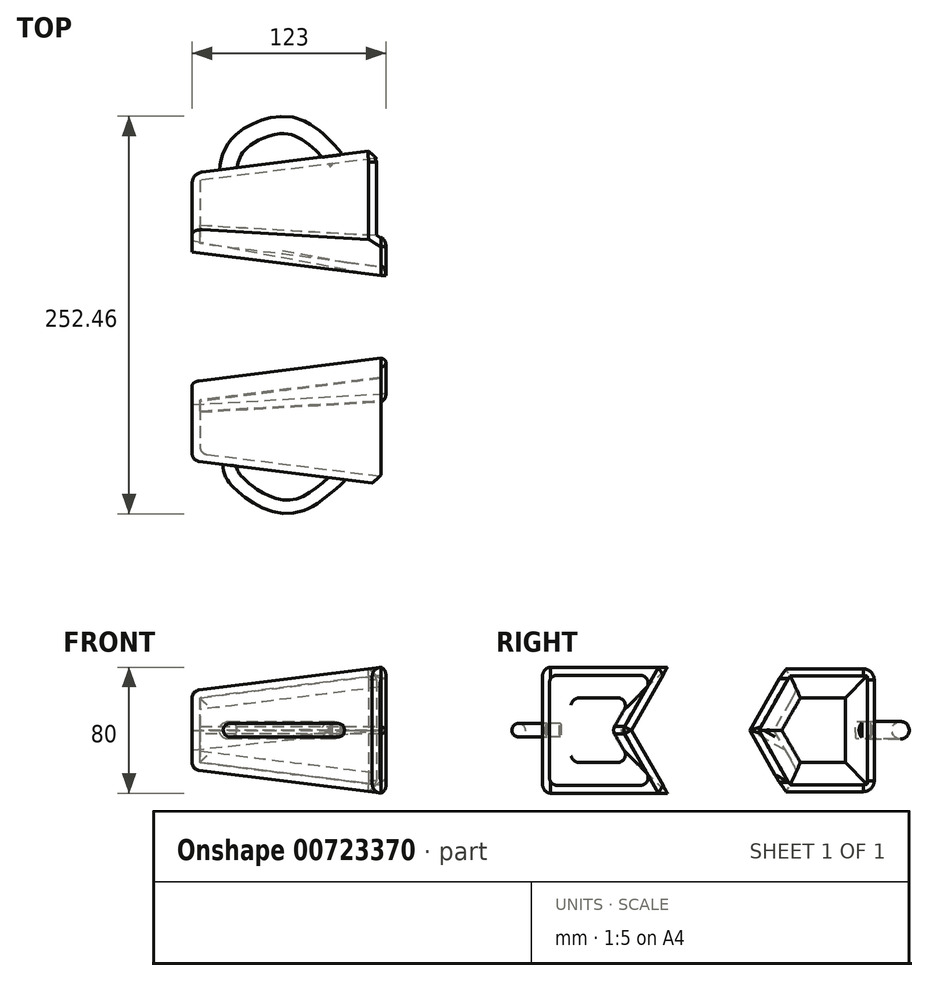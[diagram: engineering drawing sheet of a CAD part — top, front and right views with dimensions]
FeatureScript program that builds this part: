
annotation { "Feature Type Name" : "Feature", "Feature Type Description" : "" }
export const myFeature = defineFeature(function(context is Context, id is Id, definition is map)
    precondition{}
    {
        {
            var Q0;
            Q0=qCreatedBy(makeId("Right.planeOp"),FACE);
            cPlane(context, id + "F0", {"entities" : qUnion([Q0]), "cplaneType" : CPlaneType.OFFSET, "offset" : 120 * mm, "width" : 150 * mm, "height" : 150 * mm});
        }
        {
            var Q0;
            Q0=qCreatedBy(makeId("Right.planeOp"),FACE);
            var sketch = newSketch(context, id + "F1", { "sketchPlane" : qUnion([Q0])});
            skLineSegment(sketch, "E0.bottom", {"start": v(25, -25) * mm, "end": v(-25, -25) * mm});
            skLineSegment(sketch, "E0.top", {"start": v(25, 25) * mm, "end": v(-25, 25) * mm});
            skLineSegment(sketch, "E0.right", {"start": v(-25, -25) * mm, "end": v(-25, 25) * mm});
            skLineSegment(sketch, "E1.bottom", {"start": v(157.4, -25) * mm, "end": v(121.9, -25) * mm});
            skLineSegment(sketch, "E1.top", {"start": v(157.4, 25) * mm, "end": v(121.9, 25) * mm});
            skLineSegment(sketch, "E1.left", {"start": v(157.4, -25) * mm, "end": v(157.4, 25) * mm});
            skLineSegment(sketch, "E2", {"start": v(25, 25) * mm, "end": v(10.59, 0) * mm});
            skLineSegment(sketch, "E3", {"start": v(10.59, 0) * mm, "end": v(25, -25) * mm});
            skLineSegment(sketch, "E4.1.0.0", {"start": v(107.49, 0) * mm, "end": v(121.9, -25) * mm});
            skLineSegment(sketch, "E4.1.0.1", {"start": v(121.9, 25) * mm, "end": v(107.49, 0) * mm});
            skSolve(sketch);
        }
        {
            var Q0;
            Q0=qCreatedBy(id+"F0.planeOp",FACE);
            var sketch = newSketch(context, id + "F2", { "sketchPlane" : qUnion([Q0])});
            skLineSegment(sketch, "E5.bottom", {"start": v(-40, 40) * mm, "end": v(40, 40) * mm});
            skLineSegment(sketch, "E5.top", {"start": v(-40, -40) * mm, "end": v(40, -40) * mm});
            skLineSegment(sketch, "E5.left", {"start": v(-40, 40) * mm, "end": v(-40, -40) * mm});
            skPoint(sketch, "E5.middle", {"position": v(0, 0) * mm});
            skLineSegment(sketch, "E6.bottom", {"start": v(115, 40) * mm, "end": v(172.4, 40) * mm});
            skLineSegment(sketch, "E6.top", {"start": v(115, -40) * mm, "end": v(172.4, -40) * mm});
            skLineSegment(sketch, "E6.left", {"start": v(92.4, 0.1) * mm, "end": v(92.4, -0.1) * mm});
            skLineSegment(sketch, "E6.right", {"start": v(172.4, 40) * mm, "end": v(172.4, -40) * mm});
            skLineSegment(sketch, "E7", {"start": v(40, 40) * mm, "end": v(17.35, 0) * mm});
            skLineSegment(sketch, "E8", {"start": v(17.35, 0) * mm, "end": v(40, -40) * mm});
            skLineSegment(sketch, "E9.1.0.0", {"start": v(115, 40) * mm, "end": v(92.35, 0) * mm});
            skLineSegment(sketch, "E9.1.0.1", {"start": v(92.35, 0) * mm, "end": v(115, -40) * mm});
            skSolve(sketch);
        }
        {
            var Q0;
            Q0=makeQuery(id+"F1.imprint","IMPRINT",FACE,{"disambiguationData":[TD([[makeQuery(id+"F1.imprint","IMPRINT",EDGE,{"derivedFrom":sQuery(id+"F1.wireOp",EDGE,"E0.bottom")}),-1.0]])]});
            var Q1;
            Q1=makeQuery(id+"F2.imprint","IMPRINT",FACE,{"disambiguationData":[TD([[makeQuery(id+"F2.imprint","IMPRINT",EDGE,{"derivedFrom":sQuery(id+"F2.wireOp",EDGE,"E5.bottom")}),-1.0]])]});
            var Q2;
            Q2=sQuery(id+"F2.wireOp",VERTEX,"E5.top.end");
            var Q3;
            Q3=sQuery(id+"F45uSzDcTnPupgU_0.wireOp",VERTEX,"yKV4fNBH-vfpY-PDVQ-35ui-MYD5tKzPFPvu.end");
            loft(context, id + "F3", {"sheetProfilesArray" : [{ "sheetProfileEntities" : qUnion([Q0]) }, { "sheetProfileEntities" : qUnion([Q1]) }], "connections" : [{ "connectionEntities" : qUnion([Q2, Q3]), "connectionEdgeQueries" : qUnion([]), "connectionEdgeParameters" : [] }]});
        }
        {
            var Q0;
            Q0=makeQuery(id+"F1.imprint","IMPRINT",FACE,{"disambiguationData":[TD([[makeQuery(id+"F1.imprint","IMPRINT",EDGE,{"derivedFrom":sQuery(id+"F1.wireOp",EDGE,"E1.bottom")}),-1.0]])]});
            var Q1;
            {var subQ2=sQuery(id+"F2.wireOp",EDGE,"E6.bottom");Q1=makeQuery(id+"F2.imprint","IMPRINT",FACE,{"disambiguationData":[TD([[makeQuery(id+"F2.imprint","IMPRINT",EDGE,{"derivedFrom":subQ2}),-1.0]])]});}
            var Q2;
            Q2=sQuery(id+"F2.wireOp",VERTEX,"E6.bottom.start");
            var Q3;
            Q3=sQuery(id+"F1.wireOp",VERTEX,"E1.top.end");
            loft(context, id + "F4", {"sheetProfilesArray" : [{ "sheetProfileEntities" : qUnion([Q0]) }, { "sheetProfileEntities" : qUnion([Q1]) }], "matchConnections" : true, "connections" : [{ "connectionEntities" : qUnion([Q2, Q3]), "connectionEdgeQueries" : qUnion([]), "connectionEdgeParameters" : [] }]});
        }
        {
            var Q0;
            {var subQ2=sQuery(id+"F2.wireOp",EDGE,"E6.bottom");Q0=makeQuery(id+"F4.opLoft","CAP_FACE",FACE,{"disambiguationData":[OSD([makeQuery(id+"F2.imprint","IMPRINT",FACE,{"disambiguationData":[TD([[makeQuery(id+"F2.imprint","IMPRINT",EDGE,{"derivedFrom":subQ2}),-1.0]])]})])],"isStart":true});}
            shell(context, id + "F5", {"entities" : qUnion([Q0]), "thickness" : 5 * mm});
        }
        {
            var Q0;
            Q0=makeQuery(id+"F3.opLoft","CAP_FACE",FACE,{"disambiguationData":[OSD([makeQuery(id+"F2.imprint","IMPRINT",FACE,{"disambiguationData":[TD([[makeQuery(id+"F2.imprint","IMPRINT",EDGE,{"derivedFrom":sQuery(id+"F2.wireOp",EDGE,"E5.bottom")}),-1.0]])]})])],"isStart":true});
            shell(context, id + "F6", {"entities" : qUnion([Q0]), "thickness" : 5 * mm});
        }
        {
            var Q0;
            Q0=makeQuery(id+"F4.opLoft","SWEPT_EDGE",EDGE,{"disambiguationData":[OSD([sQuery(id+"F1.wireOp",EDGE,"E1.top"),sQuery(id+"F1.wireOp",EDGE,"E1.left"),sQuery(id+"F2.wireOp",EDGE,"E6.bottom"),sQuery(id+"F2.wireOp",EDGE,"E6.right")])]});
            var Q1;
            Q1=makeQuery(id+"F4.opLoft","SWEPT_EDGE",EDGE,{"disambiguationData":[OSD([sQuery(id+"F1.wireOp",EDGE,"E1.bottom"),sQuery(id+"F1.wireOp",EDGE,"E1.left"),sQuery(id+"F2.wireOp",EDGE,"E6.top"),sQuery(id+"F2.wireOp",EDGE,"E6.right")])]});
            var Q2;
            Q2=makeQuery(id+"F4.opLoft","MID_CAP_EDGE",EDGE,{"disambiguationData":[OSD([sQuery(id+"F1.wireOp",EDGE,"E1.bottom"),sQuery(id+"F1.wireOp",EDGE,"E1.top"),sQuery(id+"F1.wireOp",EDGE,"E1.left")])],"capPos":0.0});
            var Q3;
            Q3=makeQuery(id+"F4.opLoft","MID_CAP_EDGE",EDGE,{"disambiguationData":[OSD([sQuery(id+"F1.wireOp",EDGE,"E1.top"),sQuery(id+"F1.wireOp",EDGE,"E1.left"),sQuery(id+"F1.wireOp",EDGE,"E4.1.0.1")])],"capPos":0.0});
            var Q4;
            Q4=makeQuery(id+"F4.opLoft","MID_CAP_EDGE",EDGE,{"disambiguationData":[OSD([sQuery(id+"F1.wireOp",EDGE,"E1.bottom"),sQuery(id+"F1.wireOp",EDGE,"E1.left"),sQuery(id+"F1.wireOp",EDGE,"E4.1.0.0")])],"capPos":0.0});
            fillet(context, id + "F7", {"entities" : qUnion([Q0, Q1, Q2, Q3, Q4]), "radius" : 7 * mm, "tangentPropagation" : true, "allowEdgeOverflow" : false});
        }
        {
            var Q0;
            Q0=makeQuery(id+"F4.opLoft","MID_CAP_EDGE",EDGE,{"disambiguationData":[OSD([sQuery(id+"F2.wireOp",EDGE,"E6.bottom"),sQuery(id+"F2.wireOp",EDGE,"E6.top"),sQuery(id+"F2.wireOp",EDGE,"E6.right")])],"capPos":1.0});
            var Q1;
            Q1=makeQuery(id+"F4.opLoft","MID_CAP_EDGE",EDGE,{"disambiguationData":[OSD([sQuery(id+"F2.wireOp",EDGE,"E6.bottom"),sQuery(id+"F2.wireOp",EDGE,"E6.right"),sQuery(id+"F2.wireOp",EDGE,"E9.1.0.0")])],"capPos":1.0});
            var Q2;
            Q2=makeQuery(id+"F4.opLoft","MID_CAP_EDGE",EDGE,{"disambiguationData":[OSD([sQuery(id+"F2.wireOp",EDGE,"E6.top"),sQuery(id+"F2.wireOp",EDGE,"E6.right"),sQuery(id+"F2.wireOp",EDGE,"E9.1.0.1")])],"capPos":1.0});
            var Q3;
            {var subQ0=sQuery(id+"F2.wireOp",EDGE,"E6.right");var subQ2=sQuery(id+"F2.wireOp",EDGE,"E6.top");var subQ3=sQuery(id+"F2.wireOp",EDGE,"E6.bottom");Q3=makeQuery(id+"F7.opFillet","BLEND_EDGE",EDGE,{"blendedFrom":[makeQuery(id+"F4.opLoft","SWEPT_EDGE",EDGE,{"disambiguationData":[OSD([sQuery(id+"F1.wireOp",EDGE,"E1.bottom"),sQuery(id+"F1.wireOp",EDGE,"E1.left"),subQ2,subQ0])]}),makeQuery(id+"F4.opLoft","CAP_FACE",FACE,{"disambiguationData":[OSD([makeQuery(id+"F2.imprint","IMPRINT",FACE,{"disambiguationData":[TD([[makeQuery(id+"F2.imprint","IMPRINT",EDGE,{"derivedFrom":subQ3}),-1.0]])]})])],"isStart":true})],"blendedInto":[makeQuery(id+"F4.opLoft","CAP_FACE",FACE,{"disambiguationData":[OSD([makeQuery(id+"F2.imprint","IMPRINT",FACE,{"disambiguationData":[TD([[makeQuery(id+"F2.imprint","IMPRINT",EDGE,{"derivedFrom":subQ3}),-1.0]])]})])],"isStart":true})]});}
            var Q4;
            {var subQ0=sQuery(id+"F2.wireOp",EDGE,"E6.right");var subQ3=sQuery(id+"F2.wireOp",EDGE,"E6.bottom");Q4=makeQuery(id+"F7.opFillet","BLEND_EDGE",EDGE,{"blendedFrom":[makeQuery(id+"F4.opLoft","SWEPT_EDGE",EDGE,{"disambiguationData":[OSD([sQuery(id+"F1.wireOp",EDGE,"E1.top"),sQuery(id+"F1.wireOp",EDGE,"E1.left"),subQ3,subQ0])]}),makeQuery(id+"F4.opLoft","CAP_FACE",FACE,{"disambiguationData":[OSD([makeQuery(id+"F2.imprint","IMPRINT",FACE,{"disambiguationData":[TD([[makeQuery(id+"F2.imprint","IMPRINT",EDGE,{"derivedFrom":subQ3}),-1.0]])]})])],"isStart":true})],"blendedInto":[makeQuery(id+"F4.opLoft","CAP_FACE",FACE,{"disambiguationData":[OSD([makeQuery(id+"F2.imprint","IMPRINT",FACE,{"disambiguationData":[TD([[makeQuery(id+"F2.imprint","IMPRINT",EDGE,{"derivedFrom":subQ3}),-1.0]])]})])],"isStart":true})]});}
            chamfer(context, id + "F8", {"entities" : qUnion([Q0, Q1, Q2, Q3, Q4]), "width" : 7 * mm, "tangentPropagation" : true});
        }
        {
            var Q0;
            Q0=qCreatedBy(id+"F0.planeOp",FACE);
            var sketch = newSketch(context, id + "F9", { "sketchPlane" : qUnion([Q0])});
            skLineSegment(sketch, "E10", {"start": v(40, -40) * mm, "end": v(17.35, 0) * mm});
            skLineSegment(sketch, "E11", {"start": v(17.35, 0) * mm, "end": v(40, 40) * mm});
            skLineSegment(sketch, "E12", {"start": v(40, 40) * mm, "end": v(34.25, 40) * mm});
            skLineSegment(sketch, "E13", {"start": v(34.25, 40) * mm, "end": v(11.6, 0) * mm});
            skLineSegment(sketch, "E14", {"start": v(11.6, 0) * mm, "end": v(34.25, -40) * mm});
            skLineSegment(sketch, "E15", {"start": v(34.25, -40) * mm, "end": v(40, -40) * mm});
            skLineSegment(sketch, "E16", {"start": v(116.82, -33) * mm, "end": v(98.13, 0) * mm});
            skLineSegment(sketch, "E17", {"start": v(98.13, 0) * mm, "end": v(116.82, 33) * mm});
            skLineSegment(sketch, "E18", {"start": v(116.82, 33) * mm, "end": v(111.04, 33) * mm});
            skLineSegment(sketch, "E19", {"start": v(111.04, 33) * mm, "end": v(92.35, 0) * mm});
            skLineSegment(sketch, "E20", {"start": v(92.35, 0) * mm, "end": v(111.04, -33) * mm});
            skLineSegment(sketch, "E21", {"start": v(111.04, -33) * mm, "end": v(116.82, -33) * mm});
            skSolve(sketch);
        }
        {
            var Q0;
            Q0 = qSketchRegion(id + "F9", true);
            extrude(context, id + "F10", {"entities" : qUnion([Q0]), "depth" : 3 * mm, "offsetDistance" : 25 * mm});
        }
        {
            var Q0;
            Q0=makeQuery(id+"F10.opExtrude","CAP_EDGE",EDGE,{"disambiguationData":[OSD([sQuery(id+"F9.wireOp",EDGE,"E16")])],"isStart":false});
            var Q1;
            Q1=makeQuery(id+"F10.opExtrude","CAP_EDGE",EDGE,{"disambiguationData":[OSD([sQuery(id+"F9.wireOp",EDGE,"E17")])],"isStart":false});
            var Q2;
            Q2=makeQuery(id+"F10.opExtrude","CAP_EDGE",EDGE,{"disambiguationData":[OSD([sQuery(id+"F9.wireOp",EDGE,"E21")])],"isStart":false});
            var Q3;
            Q3=makeQuery(id+"F10.opExtrude","CAP_EDGE",EDGE,{"disambiguationData":[OSD([sQuery(id+"F9.wireOp",EDGE,"E13")])],"isStart":false});
            var Q4;
            Q4=makeQuery(id+"F10.opExtrude","CAP_EDGE",EDGE,{"disambiguationData":[OSD([sQuery(id+"F9.wireOp",EDGE,"E14")])],"isStart":false});
            var Q5;
            Q5=makeQuery(id+"F10.opExtrude","CAP_EDGE",EDGE,{"disambiguationData":[OSD([sQuery(id+"F9.wireOp",EDGE,"E12")])],"isStart":false});
            var Q6;
            Q6=makeQuery(id+"F10.opExtrude","CAP_EDGE",EDGE,{"disambiguationData":[OSD([sQuery(id+"F9.wireOp",EDGE,"E15")])],"isStart":false});
            fillet(context, id + "F11", {"entities" : qUnion([Q0, Q1, Q2, Q3, Q4, Q5, Q6]), "radius" : 5 * mm, "tangentPropagation" : true, "allowEdgeOverflow" : false});
        }
        {
            var Q0;
            Q0=makeQuery(id+"F6.opShell","OFFSET_EDGE",EDGE,{"disambiguationData":[OSD([sQuery(id+"F1.wireOp",EDGE,"E0.top"),sQuery(id+"F1.wireOp",EDGE,"E0.right"),sQuery(id+"F2.wireOp",EDGE,"E5.bottom"),sQuery(id+"F2.wireOp",EDGE,"E5.left")])]});
            var Q1;
            Q1=makeQuery(id+"F6.opShell","OFFSET_EDGE",EDGE,{"disambiguationData":[OSD([sQuery(id+"F1.wireOp",EDGE,"E0.bottom"),sQuery(id+"F1.wireOp",EDGE,"E0.top"),sQuery(id+"F1.wireOp",EDGE,"E0.right")])]});
            var Q2;
            Q2=makeQuery(id+"F6.opShell","OFFSET_EDGE",EDGE,{"disambiguationData":[OSD([sQuery(id+"F1.wireOp",EDGE,"E0.bottom"),sQuery(id+"F1.wireOp",EDGE,"E0.right"),sQuery(id+"F2.wireOp",EDGE,"E5.top"),sQuery(id+"F2.wireOp",EDGE,"E5.left")])]});
            var Q3;
            Q3=makeQuery(id+"F6.opShell","OFFSET_EDGE",EDGE,{"disambiguationData":[OSD([sQuery(id+"F1.wireOp",EDGE,"E0.bottom"),sQuery(id+"F1.wireOp",EDGE,"E3"),sQuery(id+"F2.wireOp",EDGE,"E5.top"),sQuery(id+"F2.wireOp",EDGE,"E8")])]});
            var Q4;
            Q4=makeQuery(id+"F6.opShell","OFFSET_EDGE",EDGE,{"disambiguationData":[OSD([sQuery(id+"F1.wireOp",EDGE,"E2"),sQuery(id+"F1.wireOp",EDGE,"E3"),sQuery(id+"F2.wireOp",EDGE,"E7"),sQuery(id+"F2.wireOp",EDGE,"E8")])]});
            var Q5;
            Q5=makeQuery(id+"F6.opShell","OFFSET_EDGE",EDGE,{"disambiguationData":[OSD([sQuery(id+"F1.wireOp",EDGE,"E0.top"),sQuery(id+"F1.wireOp",EDGE,"E2"),sQuery(id+"F2.wireOp",EDGE,"E5.bottom"),sQuery(id+"F2.wireOp",EDGE,"E7")])]});
            var Q6;
            Q6=makeQuery(id+"F11.opFillet","BLEND_EDGE",EDGE,{"blendedFrom":[makeQuery(id+"F10.opExtrude","CAP_EDGE",EDGE,{"disambiguationData":[OSD([sQuery(id+"F9.wireOp",EDGE,"E13")])],"isStart":false}),makeQuery(id+"F10.opExtrude","CAP_EDGE",EDGE,{"disambiguationData":[OSD([sQuery(id+"F9.wireOp",EDGE,"E14")])],"isStart":false})],"blendedInto":[]});
            fillet(context, id + "F12", {"entities" : qUnion([Q0, Q1, Q2, Q3, Q4, Q5, Q6]), "radius" : 5 * mm, "tangentPropagation" : true, "allowEdgeOverflow" : false});
        }
        {
            var Q0;
            Q0=makeQuery(id+"F5.opShell","OFFSET_EDGE",EDGE,{"disambiguationData":[OSD([sQuery(id+"F1.wireOp",EDGE,"E4.1.0.0"),sQuery(id+"F1.wireOp",EDGE,"E4.1.0.1"),sQuery(id+"F2.wireOp",EDGE,"E6.left"),sQuery(id+"F2.wireOp",EDGE,"E9.1.0.1")])]});
            var Q1;
            {var subQ0=sQuery(id+"F2.wireOp",EDGE,"E6.left");Q1=makeQuery(id+"F5.opShell","SHELL_CAP_EDGE",EDGE,{"derivedFrom":[makeQuery(id+"F4.opLoft","MID_CAP_VERTEX",VERTEX,{"disambiguationData":[OSD([subQ0,sQuery(id+"F2.wireOp",EDGE,"E9.1.0.0")])],"capPos":1.0}),makeQuery(id+"F4.opLoft","MID_CAP_VERTEX",VERTEX,{"disambiguationData":[OSD([subQ0,sQuery(id+"F2.wireOp",EDGE,"E9.1.0.1")])],"capPos":1.0})]});}
            var Q2;
            Q2=makeQuery(id+"F11.opFillet","BLEND_EDGE",EDGE,{"blendedFrom":[makeQuery(id+"F10.opExtrude","CAP_EDGE",EDGE,{"disambiguationData":[OSD([sQuery(id+"F9.wireOp",EDGE,"E16")])],"isStart":false}),makeQuery(id+"F10.opExtrude","CAP_EDGE",EDGE,{"disambiguationData":[OSD([sQuery(id+"F9.wireOp",EDGE,"E17")])],"isStart":false})],"blendedInto":[]});
            var Q3;
            {var subQ0=sQuery(id+"F2.wireOp",EDGE,"E9.1.0.0");var subQ1=sQuery(id+"F2.wireOp",EDGE,"E6.bottom");var subQ2=sQuery(id+"F1.wireOp",EDGE,"E4.1.0.1");var subQ3=sQuery(id+"F1.wireOp",EDGE,"E1.top");Q3=makeQuery(id+"F5.opShell","OFFSET_EDGE",EDGE,{"disambiguationData":[OSD([subQ3,subQ2,subQ1,subQ0]),TDD([makeQuery(id+"F4.opLoft","SWEPT_EDGE",EDGE,{"disambiguationData":[OSD([subQ3,subQ2,subQ1,subQ0])]})])]});}
            var Q4;
            Q4=makeQuery(id+"F5.opShell","OFFSET_EDGE",EDGE,{"disambiguationData":[OSD([sQuery(id+"F1.wireOp",EDGE,"E1.bottom"),sQuery(id+"F1.wireOp",EDGE,"E4.1.0.0"),sQuery(id+"F2.wireOp",EDGE,"E6.top"),sQuery(id+"F2.wireOp",EDGE,"E9.1.0.1")])]});
            var Q5;
            Q5=makeQuery(id+"F5.opShell","OFFSET_EDGE",EDGE,{"disambiguationData":[OSD([sQuery(id+"F1.wireOp",EDGE,"E1.bottom"),sQuery(id+"F1.wireOp",EDGE,"E1.left"),sQuery(id+"F2.wireOp",EDGE,"E6.top"),sQuery(id+"F2.wireOp",EDGE,"E6.right")])]});
            var Q6;
            Q6=makeQuery(id+"F5.opShell","OFFSET_EDGE",EDGE,{"disambiguationData":[OSD([sQuery(id+"F1.wireOp",EDGE,"E1.top"),sQuery(id+"F1.wireOp",EDGE,"E1.left"),sQuery(id+"F2.wireOp",EDGE,"E6.bottom"),sQuery(id+"F2.wireOp",EDGE,"E6.right")])]});
            fillet(context, id + "F13", {"entities" : qUnion([Q0, Q1, Q2, Q3, Q4, Q5, Q6]), "radius" : 5 * mm, "tangentPropagation" : true, "allowEdgeOverflow" : false});
        }
        {
            var Q0;
            Q0=makeQuery(id+"F3.opLoft","MID_CAP_EDGE",EDGE,{"disambiguationData":[OSD([sQuery(id+"F2.wireOp",EDGE,"E5.bottom"),sQuery(id+"F2.wireOp",EDGE,"E5.top"),sQuery(id+"F2.wireOp",EDGE,"E5.left")])],"capPos":1.0});
            chamfer(context, id + "F14", {"entities" : qUnion([Q0]), "width" : 5 * mm, "tangentPropagation" : true});
        }
        {
            var Q0;
            Q0=makeQuery(id+"F3.opLoft","SWEPT_EDGE",EDGE,{"disambiguationData":[OSD([sQuery(id+"F1.wireOp",EDGE,"E0.top"),sQuery(id+"F1.wireOp",EDGE,"E0.right"),sQuery(id+"F2.wireOp",EDGE,"E5.bottom"),sQuery(id+"F2.wireOp",EDGE,"E5.left")])]});
            var Q1;
            {var subQ0=sQuery(id+"F2.wireOp",EDGE,"E5.left");var subQ1=sQuery(id+"F2.wireOp",EDGE,"E5.bottom");Q1=makeQuery(id+"F14.opChamfer","BLEND_EDGE",EDGE,{"blendedFrom":[makeQuery(id+"F3.opLoft","MID_CAP_EDGE",EDGE,{"disambiguationData":[OSD([subQ1,subQ0,sQuery(id+"F2.wireOp",EDGE,"E7")])],"capPos":1.0}),makeQuery(id+"F3.opLoft","MID_CAP_EDGE",EDGE,{"disambiguationData":[OSD([subQ1,sQuery(id+"F2.wireOp",EDGE,"E5.top"),subQ0])],"capPos":1.0})],"blendedInto":[]});}
            var Q2;
            {var subQ0=sQuery(id+"F2.wireOp",EDGE,"E5.left");var subQ1=sQuery(id+"F2.wireOp",EDGE,"E5.top");Q2=makeQuery(id+"F14.opChamfer","BLEND_EDGE",EDGE,{"blendedFrom":[makeQuery(id+"F3.opLoft","MID_CAP_EDGE",EDGE,{"disambiguationData":[OSD([sQuery(id+"F2.wireOp",EDGE,"E5.bottom"),subQ1,subQ0])],"capPos":1.0}),makeQuery(id+"F3.opLoft","MID_CAP_EDGE",EDGE,{"disambiguationData":[OSD([subQ1,subQ0,sQuery(id+"F2.wireOp",EDGE,"E8")])],"capPos":1.0})],"blendedInto":[]});}
            var Q3;
            Q3=makeQuery(id+"F3.opLoft","SWEPT_EDGE",EDGE,{"disambiguationData":[OSD([sQuery(id+"F1.wireOp",EDGE,"E0.bottom"),sQuery(id+"F1.wireOp",EDGE,"E0.right"),sQuery(id+"F2.wireOp",EDGE,"E5.top"),sQuery(id+"F2.wireOp",EDGE,"E5.left")])]});
            fillet(context, id + "F15", {"entities" : qUnion([Q0, Q1, Q2, Q3]), "radius" : 5 * mm, "tangentPropagation" : true, "allowEdgeOverflow" : false});
        }
        {
            var Q0;
            Q0=makeQuery(id+"F3.opLoft","MID_CAP_EDGE",EDGE,{"disambiguationData":[OSD([sQuery(id+"F1.wireOp",EDGE,"E0.top"),sQuery(id+"F1.wireOp",EDGE,"E0.right"),sQuery(id+"F1.wireOp",EDGE,"E2")])],"capPos":0.0});
            var Q1;
            Q1=makeQuery(id+"F3.opLoft","MID_CAP_EDGE",EDGE,{"disambiguationData":[OSD([sQuery(id+"F1.wireOp",EDGE,"E0.bottom"),sQuery(id+"F1.wireOp",EDGE,"E0.top"),sQuery(id+"F1.wireOp",EDGE,"E0.right")])],"capPos":0.0});
            var Q2;
            Q2=makeQuery(id+"F3.opLoft","MID_CAP_EDGE",EDGE,{"disambiguationData":[OSD([sQuery(id+"F1.wireOp",EDGE,"E0.bottom"),sQuery(id+"F1.wireOp",EDGE,"E0.right"),sQuery(id+"F1.wireOp",EDGE,"E3")])],"capPos":0.0});
            fillet(context, id + "F16", {"entities" : qUnion([Q0, Q1, Q2]), "radius" : 5 * mm, "tangentPropagation" : true, "allowEdgeOverflow" : false});
        }
        {
            var Q0;
            Q0=qCreatedBy(makeId("Top.planeOp"),FACE);
            var sketch = newSketch(context, id + "F17", { "sketchPlane" : qUnion([Q0])});
            skFitSpline(sketch, "E22", {"points": [v(93.6, -34.42) * mm, v(58.66, -54.04) * mm, v(26.5, -34.89) * mm, v(24.46, -27.36) * mm], "startDerivative": vector(-74.83, -69.14) * mm, "endDerivative": vector(0.53, 35.46) * mm});
            skSolve(sketch);
        }
        {
            var Q0;
            Q0=qCreatedBy(makeId("Front.planeOp"),FACE);
            cPlane(context, id + "F18", {"entities" : qUnion([Q0]), "cplaneType" : CPlaneType.OFFSET, "offset" : 29 * mm, "width" : 150 * mm, "height" : 150 * mm});
        }
        {
            var Q0;
            Q0=qCreatedBy(id+"F18.planeOp",FACE);
            var sketch = newSketch(context, id + "F19", { "sketchPlane" : qUnion([Q0])});
            skCircle(sketch, "E23", {"center": v(24, 0) * mm, "radius": 4.28 * mm});
            skSolve(sketch);
        }
        {
            var Q0;
            Q0=makeQuery(id+"F19.imprint","IMPRINT",FACE,{"disambiguationData":[TD([[makeQuery(id+"F19.imprint","IMPRINT",EDGE,{"derivedFrom":sQuery(id+"F19.wireOp",EDGE,"E23")}),1.0]])]});
            var Q1;
            Q1=sQuery(id+"F19.wireOp",EDGE,"E23");
            var Q2;
            Q2=sQuery(id+"F17.wireOp",EDGE,"E22");
            sweep(context, id + "F20", {"operationType" : NewBodyOperationType.ADD, "profiles" : qUnion([Q0]), "surfaceProfiles" : qUnion([Q1]), "path" : qUnion([Q2])});
        }
        {
            var Q0;
            Q0=qCreatedBy(makeId("Top.planeOp"),FACE);
            var sketch = newSketch(context, id + "F21", { "sketchPlane" : qUnion([Q0])});
            skFitSpline(sketch, "E24", {"points": [v(91, 165.53) * mm, v(61.57, 187.27) * mm, v(29.42, 174.96) * mm, v(23.26, 157.85) * mm], "startDerivative": vector(-66.74, 75.62) * mm, "endDerivative": vector(-7.72, -65.87) * mm});
            skSolve(sketch);
        }
        {
            var Q0;
            Q0=qCreatedBy(makeId("Front.planeOp"),FACE);
            cPlane(context, id + "F22", {"entities" : qUnion([Q0]), "cplaneType" : CPlaneType.OFFSET, "offset" : 161 * mm, "oppositeDirection" : true, "width" : 150 * mm, "height" : 150 * mm});
        }
        {
            var Q0;
            Q0=qCreatedBy(id+"F22.planeOp",FACE);
            var sketch = newSketch(context, id + "F23", { "sketchPlane" : qUnion([Q0])});
            skCircle(sketch, "E25", {"center": v(23.08, 0) * mm, "radius": 5.57 * mm});
            skSolve(sketch);
        }
        {
            var Q0;
            Q0=makeQuery(id+"F23.imprint","IMPRINT",FACE,{"disambiguationData":[TD([[makeQuery(id+"F23.imprint","IMPRINT",EDGE,{"derivedFrom":sQuery(id+"F23.wireOp",EDGE,"E25")}),1.0]])]});
            var Q1;
            Q1=sQuery(id+"F21.wireOp",EDGE,"E24");
            sweep(context, id + "F24", {"operationType" : NewBodyOperationType.ADD, "profiles" : qUnion([Q0]), "path" : qUnion([Q1])});
        }
    });
